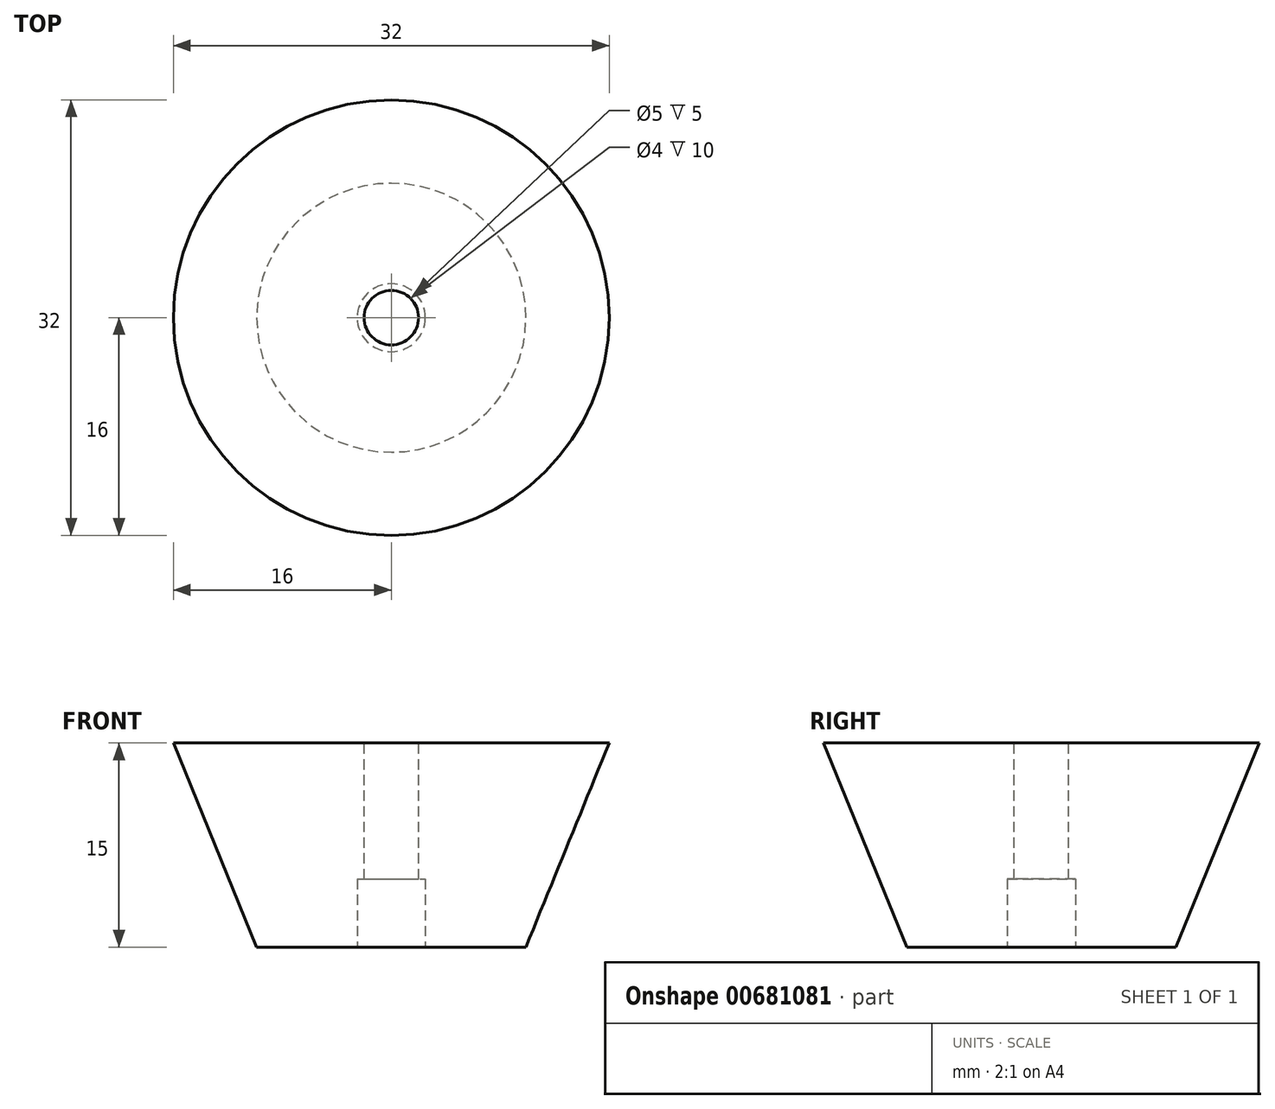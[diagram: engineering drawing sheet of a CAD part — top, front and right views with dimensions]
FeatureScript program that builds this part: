
annotation { "Feature Type Name" : "Feature", "Feature Type Description" : "" }
export const myFeature = defineFeature(function(context is Context, id is Id, definition is map)
    precondition{}
    {
        {
            var Q0;
            Q0=qCreatedBy(makeId("Right.planeOp"),FACE);
            var sketch = newSketch(context, id + "F0", { "sketchPlane" : qUnion([Q0])});
            skLineSegment(sketch, "E0", {"start": v(0, 0) * mm, "end": v(-9.88, 0) * mm});
            skLineSegment(sketch, "E1", {"start": v(-9.88, 0) * mm, "end": v(-16, 15) * mm});
            skLineSegment(sketch, "E2", {"start": v(-16, 15) * mm, "end": v(0, 15) * mm});
            skLineSegment(sketch, "E3", {"start": v(0, 15) * mm, "end": v(0, 0) * mm});
            skSolve(sketch);
        }
        {
            var Q0;
            Q0 = qSketchRegion(id + "F0", true);
            var Q1;
            Q1=sQuery(id+"F0.wireOp",EDGE,"E3");
            revolve(context, id + "F1", {"surfaceOperationType" : NewSurfaceOperationType.NEW, "entities" : qUnion([Q0]), "axis" : qUnion([Q1]), "revolveType" : RevolveType.FULL});
        }
        {
            var Q0;
            Q0=makeQuery(id+"F1.opRevolve","SWEPT_FACE",FACE,{"disambiguationData":[OSD([sQuery(id+"F0.wireOp",EDGE,"E0")])]});
            var sketch = newSketch(context, id + "F2", { "sketchPlane" : qUnion([Q0])});
            skCircle(sketch, "E4", {"center": v(0, 0) * mm, "radius": 2.5 * mm});
            skSolve(sketch);
        }
        {
            var Q0;
            Q0 = qSketchRegion(id + "F2", true);
            extrude(context, id + "F3", {"entities" : qUnion([Q0]), "operationType" : NewBodyOperationType.REMOVE, "oppositeDirection" : true, "depth" : 5 * mm, "offsetDistance" : 25 * mm});
        }
        {
            var Q0;
            Q0=makeQuery(id+"F1.opRevolve","SWEPT_FACE",FACE,{"disambiguationData":[OSD([sQuery(id+"F0.wireOp",EDGE,"E2")])]});
            var sketch = newSketch(context, id + "F4", { "sketchPlane" : qUnion([Q0])});
            skCircle(sketch, "E5", {"center": v(0, 0) * mm, "radius": 2 * mm});
            skSolve(sketch);
        }
        {
            var Q0;
            Q0 = qSketchRegion(id + "F4", true);
            var Q1;
            Q1=sQuery(id+"F4.wireOp",EDGE,"E5");
            extrude(context, id + "F5", {"entities" : qUnion([Q0]), "operationType" : NewBodyOperationType.REMOVE, "surfaceEntities" : qUnion([Q1]), "oppositeDirection" : true, "depth" : 25 * mm, "offsetDistance" : 25 * mm});
        }
    });
